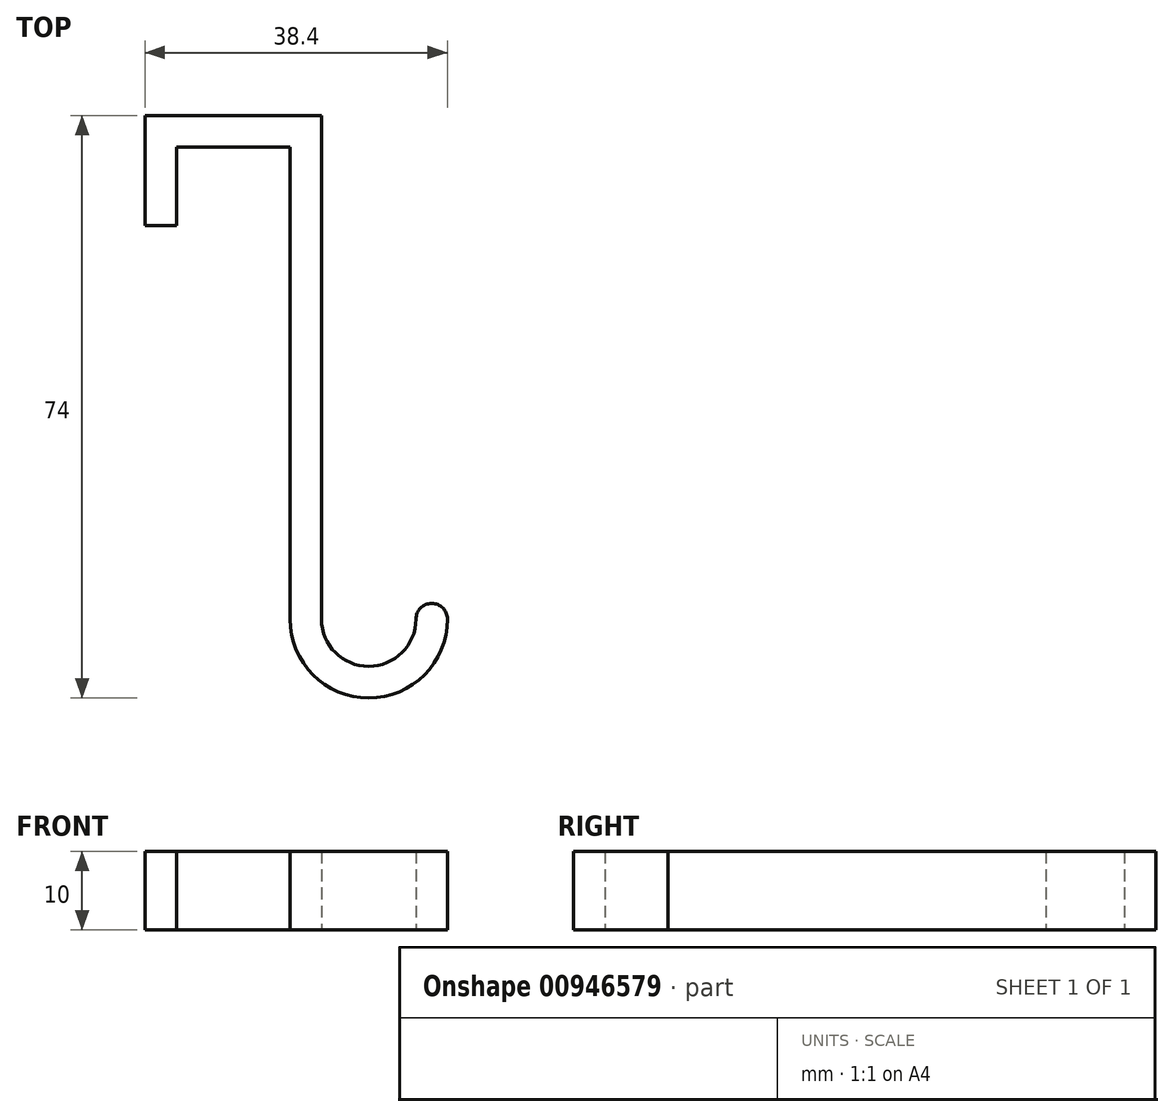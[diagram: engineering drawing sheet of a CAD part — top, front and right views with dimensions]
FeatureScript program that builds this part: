
annotation { "Feature Type Name" : "Feature", "Feature Type Description" : "" }
export const myFeature = defineFeature(function(context is Context, id is Id, definition is map)
    precondition{}
    {
        {
            var Q0;
            Q0=qCreatedBy(makeId("Top.planeOp"),FACE);
            var sketch = newSketch(context, id + "F0", { "sketchPlane" : qUnion([Q0])});
            skLineSegment(sketch, "E0", {"start": v(0, 0) * mm, "end": v(0, 10) * mm});
            skLineSegment(sketch, "E1", {"start": v(0, 10) * mm, "end": v(14.4, 10) * mm});
            skLineSegment(sketch, "E2", {"start": v(14.4, 10) * mm, "end": v(14.4, -50) * mm});
            skArc(sketch, "E3", {"start": v(14.4, -50) * mm, "mid": v(24.4, -60) * mm, "end": v(34.4, -50) * mm});
            skArc(sketch, "E4", {"start": v(30.4, -50) * mm, "mid": v(24.4, -56) * mm, "end": v(18.4, -50) * mm});
            skLineSegment(sketch, "E5", {"start": v(18.4, -50) * mm, "end": v(18.4, 14) * mm});
            skLineSegment(sketch, "E6", {"start": v(18.4, 14) * mm, "end": v(-4, 14) * mm});
            skLineSegment(sketch, "E7", {"start": v(-4, 14) * mm, "end": v(-4, 0) * mm});
            skLineSegment(sketch, "E8", {"start": v(-4, 0) * mm, "end": v(0, 0) * mm});
            skArc(sketch, "E9", {"start": v(30.4, -50) * mm, "mid": v(32.4, -48) * mm, "end": v(34.4, -50) * mm});
            skLineSegment(sketch, "E10", {"start": v(0, 10) * mm, "end": v(-4, 14) * mm, "construction": true});
            skLineSegment(sketch, "E11", {"start": v(14.4, 10) * mm, "end": v(18.4, 14) * mm, "construction": true});
            skSolve(sketch);
        }
        {
            var Q0;
            Q0=makeQuery(id+"F0.imprint","IMPRINT",FACE,{"disambiguationData":[TD([[makeQuery(id+"F0.imprint","IMPRINT",EDGE,{"derivedFrom":sQuery(id+"F0.wireOp",EDGE,"E0")}),1.0]])]});
            extrude(context, id + "F1", {"entities" : qUnion([Q0]), "depth" : 10 * mm, "offsetDistance" : 25 * mm});
        }
    });
